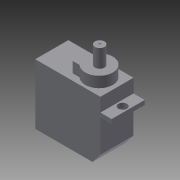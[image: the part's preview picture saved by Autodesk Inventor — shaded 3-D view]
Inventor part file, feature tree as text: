
AUTODESK INVENTOR PART (.ipt)
format: ipt  version: 2015 (Build 190159000, 159)  size: 163,328 bytes
history: native  units: in
note: dims shown in document units (in); Inventor stores cm internally (conversion verified against a paired STEP export)
features: extrude x10, sketch x10, projected_geometry x2
ambient origin geometry x8: Origin, YZ Plane, XZ Plane, XY Plane, X Axis, Y Axis, Z Axis, Center Point
bodies: Solid1 (feature_tree)
feature tree (22):
  extrude  "Extrusion1"  Depth=0.91in
  extrude  "Extrusion2"  Depth=0.462in TaperAngle=0.0deg
  extrude  "Extrusion3"  Depth=0.06in
  extrude  "Extrusion4"  Depth=0.19in
  extrude  "Extrusion5"  Depth=0.3855in
  extrude  "Extrusion6"  Depth=0.15in TaperAngle=0.0deg
  extrude  "Extrusion7"  Depth=0.25in TaperAngle=0.0deg
  extrude  "Extrusion8"  Depth=0.01in
  extrude  "Extrusion9"  Depth=0.1571in
  extrude  "Extrusion10"  Depth=0.462in
  sketch  "Sketch1"  dims[d0=0.592in d1=0.91in]
  sketch  "Sketch2"  dims[d2=0.462in d3=0.0in d4=0.462in d5=0.0in]
  sketch  "Sketch3"  dims[d6=1.25in d7=0.06in]
  sketch  "Sketch4"  dims[d8=0.462in d9=0.0in d10=0.19in]
  sketch  "Sketch5"  dims[d11=0.5in d12=0.0in d14=0.3855in]
  sketch  "Sketch6"  dims[d15=0.15in d16=0.0in d17=0.157in d18=0.0in]
  sketch  "Sketch7"  dims[d19=0.135in d20=0.25in d21=0.0in]
  sketch  "Sketch8"  dims[d22=0.01in d23=0.0in d24=0.1828in]
  sketch  "Sketch9"  dims[d25=0.1571in d26=0.12in]
  projected_geometry  "Projected Loop1"
  sketch  "Sketch11"  dims[d27=0.0915in d28=0.462in d29=0.231in d30=0.12in d31=0.231in d32=0.0785in d33=1.0in d34=0.0in d35=0.0962in d36=0.1404in d37=0.04in d38=0.0367in d39=0.462in d40=0.231in d46=0.66in d47=1.0in d48=0.0in]
  projected_geometry  "Projected Loop5"
